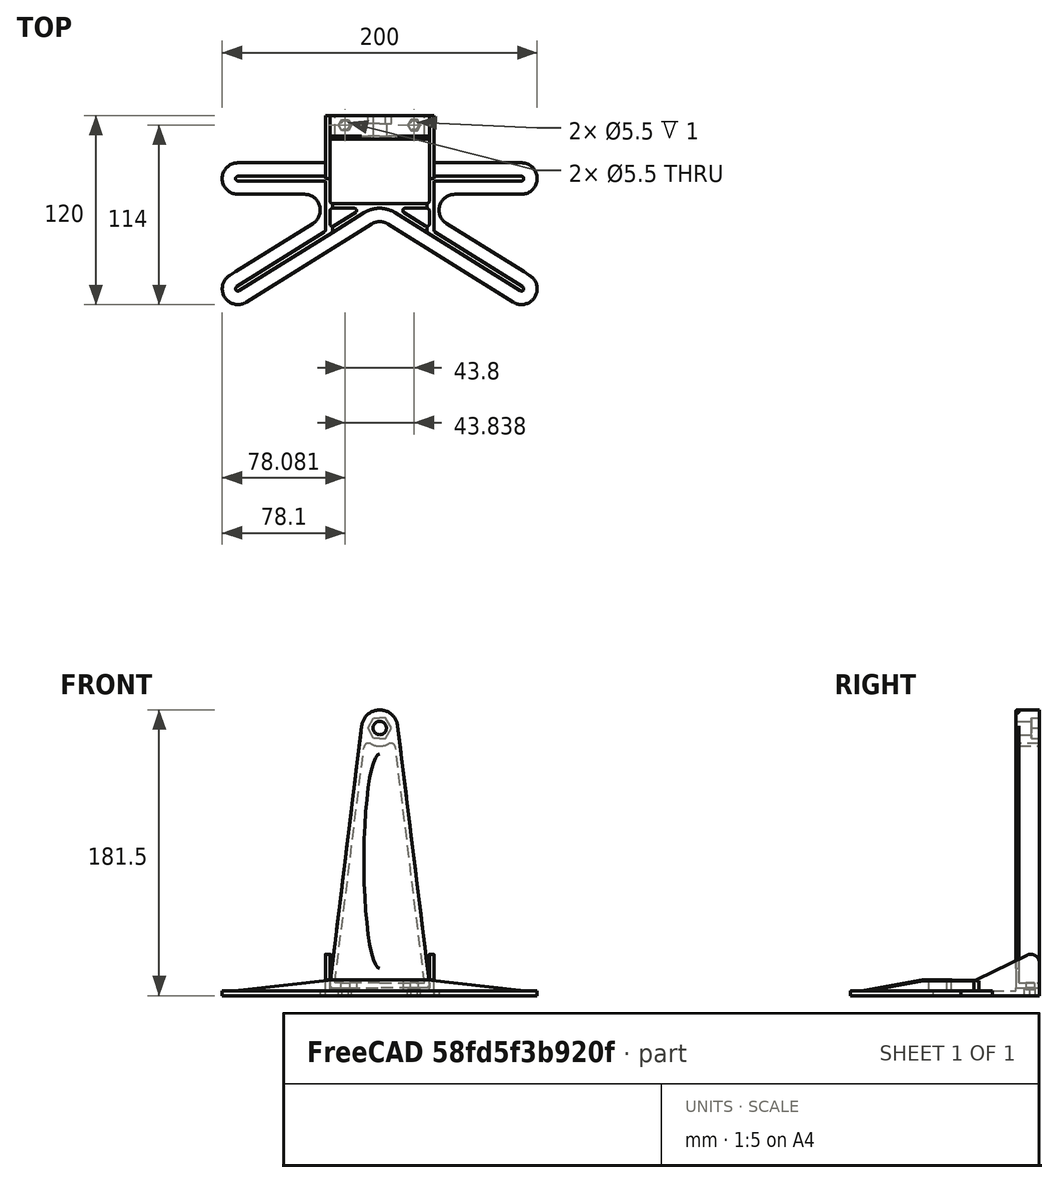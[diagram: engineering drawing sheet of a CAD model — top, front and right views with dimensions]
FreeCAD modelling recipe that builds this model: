
FCSTD DOCUMENT  (FreeCAD 0.19R24366 (Git))
Label: Ferris wheel foundation
License: All rights reserved
LicenseURL: http://en.wikipedia.org/wiki/All_rights_reserved
objects: Sketcher::SketchObject×14, PartDesign::Pad×6, PartDesign::Pocket×5, PartDesign::Mirrored×2, PartDesign::Body×2, PartDesign::SubtractivePipe×1, Mesh::Feature×1
note: 42 computed .brp shape members not serialized (recipe doc carries the construction recipe); baked Part::Feature solids carry a one-line shape summary decoded from their .brp

FEATURE [Sketcher::SketchObject] Sketch
  FullyConstrained = true
  MapMode = 5
  Support = -> [XY_Plane]
  sketch-geometry (16):
    g0: LineSegment StartX=0 StartY=0 StartZ=0 EndX=90 EndY=0 EndZ=0
    g1: LineSegment StartX=10 StartY=-20 StartZ=0 EndX=90 EndY=-70 EndZ=0
    g2: ArcOfCircle CenterX=90 CenterY=0 CenterZ=0 NormalX=0 NormalY=0 NormalZ=1 AngleXU=0 Radius=10 StartAngle=4.71239 EndAngle=7.85398
    g3: ArcOfCircle CenterX=90 CenterY=-70 CenterZ=0 NormalX=0 NormalY=0 NormalZ=1 AngleXU=0 Radius=10 StartAngle=4.15379 EndAngle=7.29539
    g4: ArcOfCircle CenterX=47.7359 CenterY=-20 CenterZ=0 NormalX=0 NormalY=0 NormalZ=1 AngleXU=0 Radius=10 StartAngle=1.5708 EndAngle=4.15379
    g5: ArcOfCircle CenterX=0 CenterY=-37.335 CenterZ=0 NormalX=0 NormalY=0 NormalZ=1 AngleXU=0 Radius=10 StartAngle=1.01219 EndAngle=1.5708
    g6: LineSegment StartX=47.7359 StartY=-10 StartZ=0 EndX=90 EndY=-10 EndZ=0
    g7: LineSegment StartX=42.436 StartY=-28.48 StartZ=0 EndX=95.3 EndY=-61.52 EndZ=0
    g8: LineSegment StartX=84.7 StartY=-78.48 StartZ=0 EndX=5.30001 EndY=-28.855 EndZ=0
    g9: LineSegment StartX=90 StartY=10 StartZ=0 EndX=31.5 EndY=10 EndZ=0
    g10: LineSegment StartX=0 StartY=10 StartZ=0 EndX=0 EndY=-27.335 EndZ=0
    g11: LineSegment StartX=10 StartY=-20 StartZ=0 EndX=0 EndY=-20 EndZ=0
    g12: LineSegment StartX=90 StartY=0 StartZ=0 EndX=100 EndY=0 EndZ=0
    g13: LineSegment StartX=31.5 StartY=10 StartZ=0 EndX=31.5 EndY=40 EndZ=0
    g14: LineSegment StartX=31.5 StartY=40 StartZ=0 EndX=0 EndY=40 EndZ=0
    g15: LineSegment StartX=0 StartY=40 StartZ=0 EndX=0 EndY=10 EndZ=0
  constraints (51):
    c: Coincident(g0,g-1)
    c: PointOnObject(g0,g-1)
    c: DistanceX(g0) = 90
    c: DistanceY(g1) = -70
    c: Vertical(g0,g1)
    c: Coincident(g2,g0)
    c: Coincident(g3,g1)
    c: PointOnObject(g5,g-2)
    c: PointOnObject(g5,g-2)
    c: Coincident(g6,g4)
    c: Coincident(g6,g2)
    c: Horizontal(g6)
    c: Coincident(g7,g4)
    c: Coincident(g7,g3)
    c: Coincident(g8,g3)
    c: Coincident(g8,g5)
    c: Coincident(g9,g2)
    c: PointOnObject(g10,g-2)
    c: Horizontal(g9)
    c: Coincident(g10,g5)
    c: Tangent(g2,g9)
    c: Tangent(g2,g6)
    c: Tangent(g4,g6)
    c: Tangent(g4,g7)
    c: Tangent(g7,g3)
    c: Tangent(g3,g8)
    c: Tangent(g8,g5)
    c: Parallel(g7,g1)
    c: Parallel(g1,g8)
    c: Equal(g5,g3)
    c: Equal(g3,g4)
    c: Equal(g4,g2)
    c: Horizontal(g4,g1)
    c: Diameter(g3) = 20
    c: Coincident(g11,g1)
    c: PointOnObject(g11,g10)
    c: Horizontal(g11)
    c: Coincident(g12,g2)
    c: PointOnObject(g12,g2)
    c: Horizontal(g12)
    c: Equal(g12,g11)
    c: Vertical(g13)
    c: Coincident(g14,g13)
    c: PointOnObject(g14,g-2)
    c: Horizontal(g14)
    c: Distance(g14) = 31.5
    c: Coincident(g15,g14)
    c: Coincident(g15,g10)
    c: Coincident(g9,g13)
    c: Distance(g15) = 30
    c: Horizontal(g10,g9)
FEATURE [Sketcher::SketchObject] Sketch001
  FullyConstrained = true
  MapMode = 5
  Support = -> [XY_Plane]
  expr: Constraints[34] = Sketch.Constraints[33]
  expr: Constraints[3] = Sketch.Constraints[3]
  expr: Constraints[2] = Sketch.Constraints[2]
  sketch-geometry (34):
    g0: LineSegment StartX=0 StartY=0 StartZ=0 EndX=90 EndY=0 EndZ=0
    g1: LineSegment StartX=10 StartY=-20 StartZ=0 EndX=90 EndY=-70 EndZ=0
    g2: ArcOfCircle CenterX=90 CenterY=0 CenterZ=0 NormalX=0 NormalY=0 NormalZ=1 AngleXU=0 Radius=10 StartAngle=4.71239 EndAngle=7.85398
    g3: ArcOfCircle CenterX=90 CenterY=-70 CenterZ=0 NormalX=0 NormalY=0 NormalZ=1 AngleXU=0 Radius=10 StartAngle=4.15379 EndAngle=7.29538
    g4: ArcOfCircle CenterX=47.7359 CenterY=-20 CenterZ=0 NormalX=0 NormalY=0 NormalZ=1 AngleXU=0 Radius=10 StartAngle=1.5708 EndAngle=4.15379
    g5: ArcOfCircle CenterX=0 CenterY=-37.335 CenterZ=0 NormalX=0 NormalY=0 NormalZ=1 AngleXU=0 Radius=10 StartAngle=1.0122 EndAngle=1.5708
    g6: LineSegment StartX=47.7359 StartY=-10 StartZ=0 EndX=90 EndY=-10 EndZ=0
    g7: LineSegment StartX=42.4359 StartY=-28.48 StartZ=0 EndX=95.3 EndY=-61.52 EndZ=0
    g8: LineSegment StartX=84.7 StartY=-78.48 StartZ=0 EndX=5.29999 EndY=-28.855 EndZ=0
    g9: LineSegment StartX=90 StartY=10 StartZ=0 EndX=0 EndY=10 EndZ=0
    g10: LineSegment StartX=0 StartY=10 StartZ=0 EndX=0 EndY=-27.335 EndZ=0
    g11: LineSegment StartX=10 StartY=-20 StartZ=0 EndX=0 EndY=-20 EndZ=0
    g12: LineSegment StartX=90 StartY=0 StartZ=0 EndX=100 EndY=0 EndZ=0
    g13: ArcOfCircle CenterX=90 CenterY=-70 CenterZ=0 NormalX=0 NormalY=0 NormalZ=1 AngleXU=0 Radius=1.5 StartAngle=4.15379 EndAngle=7.29538
    g14: ArcOfCircle CenterX=90 CenterY=0 CenterZ=0 NormalX=0 NormalY=0 NormalZ=1 AngleXU=0 Radius=1.5 StartAngle=4.71239 EndAngle=7.85398
    g15: ArcOfCircle CenterX=0 CenterY=-37.335 CenterZ=0 NormalX=0 NormalY=0 NormalZ=1 AngleXU=0 Radius=18.5 StartAngle=1.0122 EndAngle=1.5708
    g16: LineSegment StartX=34.5 StartY=-1.5 StartZ=0 EndX=90 EndY=-1.5 EndZ=0
    g17: LineSegment StartX=90.795 StartY=-68.728 StartZ=0 EndX=35.205 EndY=-33.9843 EndZ=0
    g18: LineSegment StartX=89.205 StartY=-71.272 StartZ=0 EndX=9.80498 EndY=-21.647 EndZ=0
    g19: LineSegment StartX=90 StartY=1.5 StartZ=0 EndX=34.5 EndY=1.5 EndZ=0
    g20: LineSegment StartX=0 StartY=-15.835 StartZ=0 EndX=30 EndY=-15.835 EndZ=0
    g21: ArcOfCircle CenterX=30 CenterY=-14.335 CenterZ=0 NormalX=0 NormalY=0 NormalZ=1 AngleXU=0 Radius=1.5 StartAngle=4.71239 EndAngle=6.28319
    g22: LineSegment StartX=1.1e-15 StartY=-18.835 StartZ=0 EndX=0 EndY=-15.835 EndZ=0
    g23: LineSegment StartX=15.4013 StartY=-21.607 StartZ=0 EndX=29.205 EndY=-30.2343 EndZ=0
    g24: LineSegment StartX=16.1963 StartY=-18.835 StartZ=0 EndX=30 EndY=-18.835 EndZ=0
    g25: ArcOfCircle CenterX=16.1963 CenterY=-20.335 CenterZ=0 NormalX=0 NormalY=0 NormalZ=1 AngleXU=0 Radius=1.5 StartAngle=1.5708 EndAngle=4.15379
    g26: ArcOfCircle CenterX=30 CenterY=-20.335 CenterZ=0 NormalX=0 NormalY=0 NormalZ=1 AngleXU=0 Radius=1.5 StartAngle=3.41034e-06 EndAngle=1.5708
    g27: ArcOfCircle CenterX=30 CenterY=-28.9623 CenterZ=0 NormalX=0 NormalY=0 NormalZ=1 AngleXU=0 Radius=1.5 StartAngle=4.15379 EndAngle=6.28319
    g28: LineSegment StartX=34.5 StartY=40 StartZ=0 EndX=31.5 EndY=40 EndZ=0
    g29: LineSegment StartX=31.5 StartY=40 StartZ=0 EndX=31.5 EndY=-14.335 EndZ=0
    g30: LineSegment StartX=34.5 StartY=1.5 StartZ=0 EndX=34.5 EndY=40 EndZ=0
    g31: LineSegment StartX=34.5 StartY=-32.7123 StartZ=0 EndX=34.5 EndY=-1.5 EndZ=0
    g32: ArcOfCircle CenterX=36 CenterY=-32.7123 CenterZ=0 NormalX=0 NormalY=0 NormalZ=1 AngleXU=0 Radius=1.5 StartAngle=3.14159 EndAngle=4.15379
    g33: LineSegment StartX=31.5 StartY=-20.3349 StartZ=0 EndX=31.5 EndY=-28.9623 EndZ=0
  constraints (109):
    c: Coincident(g0,g-1)
    c: PointOnObject(g0,g-1)
    c: DistanceX(g0) = 90
    c: DistanceY(g1) = -70
    c: Vertical(g0,g1)
    c: Coincident(g2,g0)
    c: Coincident(g3,g1)
    c: PointOnObject(g5,g-2)
    c: PointOnObject(g5,g-2)
    c: Coincident(g6,g4)
    c: Coincident(g6,g2)
    c: Horizontal(g6)
    c: Coincident(g7,g4)
    c: Coincident(g7,g3)
    c: Coincident(g8,g3)
    c: Coincident(g8,g5)
    c: Coincident(g9,g2)
    c: PointOnObject(g9,g-2)
    c: Horizontal(g9)
    c: Coincident(g10,g9)
    c: Coincident(g10,g5)
    c: Tangent(g2,g9)
    c: Tangent(g2,g6)
    c: Tangent(g4,g6)
    c: Tangent(g4,g7)
    c: Tangent(g7,g3)
    c: Tangent(g3,g8)
    c: Tangent(g8,g5)
    c: Parallel(g7,g1)
    c: Parallel(g1,g8)
    c: Equal(g5,g3)
    c: Equal(g3,g4)
    c: Equal(g4,g2)
    c: Horizontal(g4,g1)
    c: Diameter(g3) = 20
    c: Coincident(g11,g1)
    c: PointOnObject(g11,g10)
    c: Horizontal(g11)
    c: Coincident(g12,g2)
    c: PointOnObject(g12,g2)
    c: Horizontal(g12)
    c: Equal(g12,g11)
    c: Coincident(g13,g1)
    c: Coincident(g14,g0)
    c: Coincident(g15,g5)
    c: PointOnObject(g15,g10)
    c: Coincident(g16,g14)
    c: Horizontal(g16)
    c: Coincident(g17,g13)
    c: Coincident(g18,g13)
    c: Coincident(g18,g15)
    c: Parallel(g17,g1)
    c: Parallel(g18,g1)
    c: Tangent(g13,g17)
    c: Tangent(g13,g18)
    c: Diameter(g13) = 3
    c: Equal(g13,g14)
    c: Tangent(g14,g16)
    c: Coincident(g19,g14)
    c: Horizontal(g19)
    c: PointOnObject(g20,g10)
    c: Horizontal(g20)
    c: Coincident(g21,g20)
    c: Tangent(g18,g15)
    c: Tangent(g20,g21)
    c: Coincident(g22,g15)
    c: Coincident(g22,g20)
    c: Distance(g22) = 3
    c: Coincident(g25,g24)
    c: Coincident(g25,g23)
    c: Coincident(g26,g24)
    c: Coincident(g27,g23)
    c: Tangent(g24,g25)
    c: Tangent(g25,g23)
    c: Tangent(g24,g26)
    c: Tangent(g27,g23)
    c: Horizontal(g24)
    c: Equal(g26,g25)
    c: Equal(g25,g27)
    c: Tangent(g17,g23)
    c: Equal(g27,g13)
    c: PointOnObject(g15,g24)
    c: Tangent(g14,g19)
    c: Equal(g26,g21)
    c: Coincident(g28,g29)
    c: Coincident(g30,g28)
    c: Horizontal(g28)
    c: Vertical(g29)
    c: Vertical(g30)
    c: DistanceY(g28) = 40
    c: Distance(g28) = 3
    c: DistanceX(g28) = 31.5
    c: Coincident(g21,g29)
    c: Coincident(g19,g30)
    c: Vertical(g31)
    c: Coincident(g31,g16)
    c: Vertical(g16,g19)
    c: Tangent(g21,g29)
    c: Coincident(g32,g17)
    c: Coincident(g32,g31)
    c: Tangent(g17,g32)
    c: Tangent(g32,g31)
    c: Coincident(g33,g26)
    c: Vertical(g33)
    c: Vertical(g21,g26)
    c: Coincident(g27,g33)
    c: Tangent(g33,g27)
    c: Equal(g32,g27)
    c: Tangent(g33,g26)
FEATURE [PartDesign::Pad] Pad
  Direction = (1,1,1)
  Length = 3
  Length2 = 100
  Profile = -> Sketch
  Type = 0
FEATURE [PartDesign::Pad] Pad001
  BaseFeature = -> Pad
  Direction = (1,1,1)
  Length = 10
  Length2 = 100
  Profile = -> Sketch001
  Type = 0
FEATURE [Sketcher::SketchObject] Sketch002
  FullyConstrained = true
  MapMode = 5
  Placement = pos=(0,0,0) rot=(1,0,0;1.5708rad)
  Support = -> [XZ_Plane001]
  sketch-geometry (21):
    g0: LineSegment StartX=7.50555 StartY=165 StartZ=0 EndX=3.75278 EndY=171.5 EndZ=0
    g1: LineSegment StartX=3.75278 StartY=171.5 StartZ=0 EndX=-3.75278 EndY=171.5 EndZ=0
    g2: LineSegment StartX=-3.75278 StartY=171.5 StartZ=0 EndX=-7.50555 EndY=165 EndZ=0
    g3: LineSegment StartX=-7.50555 StartY=165 StartZ=0 EndX=-3.75278 EndY=158.5 EndZ=0
    g4: LineSegment StartX=-3.75278 StartY=158.5 StartZ=0 EndX=3.75278 EndY=158.5 EndZ=0
    g5: LineSegment StartX=3.75278 StartY=158.5 StartZ=0 EndX=7.50555 EndY=165 EndZ=0
    g6: Circle CenterX=0 CenterY=165 CenterZ=0 NormalX=0 NormalY=0 NormalZ=1 AngleXU=0 Radius=7.50555
    g7: ArcOfCircle CenterX=0 CenterY=165 CenterZ=0 NormalX=0 NormalY=0 NormalZ=1 AngleXU=0 Radius=11.5 StartAngle=0.122446 EndAngle=1.5708
    g8: LineSegment StartX=11.4139 StartY=166.405 StartZ=0 EndX=31.4775 EndY=3.36703 EndZ=0
    g9: LineSegment StartX=31.5 StartY=3 StartZ=0 EndX=31.5 EndY=0 EndZ=0
    g10: ArcOfCircle CenterX=28.495 CenterY=3 CenterZ=0 NormalX=0 NormalY=0 NormalZ=1 AngleXU=0 Radius=3.005 StartAngle=6.28319 EndAngle=6.40563
    g11: ArcOfEllipse CenterX=0 CenterY=80.375 CenterZ=0 NormalX=0 NormalY=0 NormalZ=1 MajorRadius=68.125 MinorRadius=10 AngleXU=-1.5708 StartAngle=0 EndAngle=3.14159
    g12: LineSegment StartX=0 StartY=12.25 StartZ=0 EndX=0 EndY=148.5 EndZ=0
    g13: LineSegment StartX=10 StartY=80.375 StartZ=0 EndX=-10 EndY=80.375 EndZ=0
    g14: GeomPoint X=0 Y=12.9879 Z=0
    g15: GeomPoint X=0 Y=147.762 Z=0
    g16: LineSegment StartX=31.5 StartY=0 StartZ=0 EndX=0 EndY=0 EndZ=0
    g17: LineSegment StartX=0 StartY=12.25 StartZ=0 EndX=0 EndY=0 EndZ=0
    g18: LineSegment StartX=1.2e-15 StartY=148.5 StartZ=0 EndX=-8e-16 EndY=160.75 EndZ=0
    g19: LineSegment StartX=0 StartY=176.5 StartZ=0 EndX=0 EndY=169.25 EndZ=0
    g20: ArcOfCircle CenterX=0 CenterY=165 CenterZ=0 NormalX=0 NormalY=0 NormalZ=1 AngleXU=0 Radius=4.25 StartAngle=4.71239 EndAngle=7.85398
  constraints (52):
    c: Coincident(g0,g1)
    c: Coincident(g1,g2)
    c: Coincident(g2,g3)
    c: Coincident(g3,g4)
    c: Coincident(g4,g5)
    c: Coincident(g5,g0)
    c: Equal(g0, g1-g5) x5
    c: PointOnObject(g0,g6)
    c: PointOnObject(g1,g6)
    c: PointOnObject(g2,g6)
    c: PointOnObject(g3,g6)
    c: PointOnObject(g4,g6)
    c: PointOnObject(g5,g6)
    c: PointOnObject(g6,g-2)
    c: Horizontal(g1)
    c: DistanceY(g4,g0) = 13
    c: Coincident(g7,g6)
    c: PointOnObject(g7,g-2)
    c: Coincident(g8,g7)
    c: PointOnObject(g9,g-1)
    c: Vertical(g9)
    c: Coincident(g10,g9)
    c: Coincident(g10,g8)
    c: InternalAlignment(g12-g15 -> g11) x4
    c: PointOnObject(g11,g-2)
    c: PointOnObject(g11,g-2)
    c: Vertical(g12)
    c: Distance(g13) = 20
    c: DistanceY(g7) = 165
    c: Diameter(g6) = 15.0111
    c: Diameter(g7) = 23
    c: Tangent(g8,g7)
    c: Coincident(g16,g9)
    c: Coincident(g16,g-1)
    c: PointOnObject(g11,g-2)
    c: Coincident(g17,g11)
    c: Coincident(g17,g16)
    c: Coincident(g18,g11)
    c: PointOnObject(g18,g-2)
    c: Coincident(g19,g7)
    c: PointOnObject(g19,g-2)
    c: Coincident(g20,g7)
    c: Coincident(g20,g18)
    c: Coincident(g20,g19)
    c: Diameter(g20) = 8.5
    c: Distance(g16) = 31.5
    c: Distance(g11,g4) = 10
    c: Equal(g17,g18)
    c: Tangent(g10,g8)
    c: Tangent(g10,g9)
    c: Distance(g9) = 3
    c: Diameter(g10) = 6.01
FEATURE [Sketcher::SketchObject] Sketch003
  AttachmentOffset = pos=(0,0,2) rot=(0,0,1;0rad)
  FullyConstrained = true
  MapMode = 5
  Placement = pos=(0,-2,4e-16) rot=(1,0,0;1.5708rad)
  Support = -> [XZ_Plane001]
  expr: .AttachmentOffset.Base.z = Pad002.Length
  expr: Constraints[52] = Sketch002.Constraints[57]
  expr: Constraints[48] = Sketch002.Constraints[53]
  expr: Constraints[15] = Sketch002.Constraints[19]
  expr: Constraints[33] = Sketch002.Constraints[37]
  expr: Constraints[46] = Sketch002.Constraints[51]
  expr: Constraints[47] = Sketch002.Constraints[52]
  expr: Constraints[31] = Sketch002.Constraints[35]
  expr: Constraints[30] = Sketch002.Constraints[34]
  sketch-geometry (31):
    g0: LineSegment StartX=7.50555 StartY=165 StartZ=0 EndX=3.75278 EndY=171.5 EndZ=0
    g1: LineSegment StartX=3.75278 StartY=171.5 StartZ=0 EndX=0 EndY=171.5 EndZ=0
    g2: LineSegment StartX=-3.75278 StartY=171.5 StartZ=0 EndX=-7.50555 EndY=165 EndZ=0
    g3: LineSegment StartX=-7.50555 StartY=165 StartZ=0 EndX=-3.75278 EndY=158.5 EndZ=0
    g4: LineSegment StartX=0 StartY=158.5 StartZ=0 EndX=3.75278 EndY=158.5 EndZ=0
    g5: LineSegment StartX=3.75278 StartY=158.5 StartZ=0 EndX=7.50555 EndY=165 EndZ=0
    g6: Circle CenterX=0 CenterY=165 CenterZ=0 NormalX=0 NormalY=0 NormalZ=1 AngleXU=0 Radius=7.50555
    g7: ArcOfCircle CenterX=0 CenterY=165 CenterZ=0 NormalX=0 NormalY=0 NormalZ=1 AngleXU=0 Radius=11.5 StartAngle=0.122445 EndAngle=1.5708
    g8: LineSegment StartX=11.4139 StartY=166.405 StartZ=0 EndX=31.4775 EndY=3.36642 EndZ=0
    g9: LineSegment StartX=31.5 StartY=3 StartZ=0 EndX=31.5 EndY=0 EndZ=0
    g10: ArcOfCircle CenterX=28.5 CenterY=3 CenterZ=0 NormalX=0 NormalY=0 NormalZ=1 AngleXU=0 Radius=3 StartAngle=6.28319 EndAngle=6.40563
    g11: ArcOfEllipse CenterX=0 CenterY=80.375 CenterZ=0 NormalX=0 NormalY=0 NormalZ=1 MajorRadius=68.125 MinorRadius=10 AngleXU=-1.5708 StartAngle=0 EndAngle=3.14159
    g12: LineSegment StartX=0 StartY=12.25 StartZ=0 EndX=0 EndY=148.5 EndZ=0
    g13: LineSegment StartX=10 StartY=80.375 StartZ=0 EndX=-10 EndY=80.375 EndZ=0
    g14: GeomPoint X=0 Y=12.9879 Z=0
    g15: GeomPoint X=0 Y=147.762 Z=0
    g16: LineSegment StartX=31.5 StartY=0 StartZ=0 EndX=0 EndY=0 EndZ=0
    g17: LineSegment StartX=0 StartY=12.25 StartZ=0 EndX=0 EndY=0 EndZ=0
    g18: LineSegment StartX=0 StartY=148.5 StartZ=0 EndX=0 EndY=160.75 EndZ=0
    g19: LineSegment StartX=0 StartY=176.5 StartZ=0 EndX=0 EndY=171.5 EndZ=0
    g20: ArcOfCircle CenterX=0 CenterY=165 CenterZ=0 NormalX=0 NormalY=0 NormalZ=1 AngleXU=0 Radius=4.25 StartAngle=4.71239 EndAngle=7.85398
    g21: LineSegment StartX=-3.75278 StartY=171.5 StartZ=0 EndX=-3.75278 EndY=158.5 EndZ=0
    g22: LineSegment StartX=3.75278 StartY=158.5 StartZ=0 EndX=-7.50555 EndY=165 EndZ=0
    g23: LineSegment StartX=0 StartY=0 StartZ=0 EndX=0 EndY=3 EndZ=0
    g24: LineSegment StartX=0 StartY=3 StartZ=0 EndX=28.5 EndY=3 EndZ=0
    g25: LineSegment StartX=28.5 StartY=3 StartZ=0 EndX=10.075 EndY=152.722 EndZ=0
    g26: ArcOfCircle CenterX=0 CenterY=165 CenterZ=0 NormalX=0 NormalY=0 NormalZ=1 AngleXU=0 Radius=11.5 StartAngle=4.71239 EndAngle=5.22389
    g27: ArcOfCircle CenterX=7.0975 CenterY=152.356 CenterZ=0 NormalX=0 NormalY=0 NormalZ=1 AngleXU=0 Radius=3 StartAngle=0.122445 EndAngle=2.08229
    g28: LineSegment StartX=0 StartY=153.5 StartZ=0 EndX=0 EndY=158.5 EndZ=0
    g29: LineSegment StartX=0 StartY=171.5 StartZ=0 EndX=0 EndY=169.25 EndZ=0
    g30: LineSegment StartX=0 StartY=160.75 StartZ=0 EndX=0 EndY=158.5 EndZ=0
  constraints (83):
    c: Coincident(g0,g1)
    c: Coincident(g2,g3)
    c: Coincident(g4,g5)
    c: Coincident(g5,g0)
    c: Equal(g0,g2)
    c: Equal(g0,g3)
    c: Equal(g0,g5)
    c: PointOnObject(g0,g6)
    c: PointOnObject(g2,g6)
    c: PointOnObject(g2,g6)
    c: PointOnObject(g3,g6)
    c: PointOnObject(g4,g6)
    c: PointOnObject(g5,g6)
    c: PointOnObject(g6,g-2)
    c: Horizontal(g1)
    c: DistanceY(g4,g0) = 13
    c: Coincident(g7,g6)
    c: PointOnObject(g7,g-2)
    c: Coincident(g8,g7)
    c: PointOnObject(g9,g-1)
    c: Vertical(g9)
    c: Coincident(g10,g9)
    c: Coincident(g10,g8)
    c: InternalAlignment(g12-g15 -> g11) x4
    c: PointOnObject(g11,g-2)
    c: PointOnObject(g11,g-2)
    c: Vertical(g12)
    c: Distance(g13) = 20
    c: DistanceY(g7) = 165
    c: Diameter(g6) = 15.0111
    c: Diameter(g7) = 23
    c: Tangent(g8,g7)
    c: Coincident(g16,g9)
    c: Coincident(g16,g-1)
    c: PointOnObject(g11,g-2)
    c: Coincident(g17,g11)
    c: Coincident(g17,g16)
    c: Coincident(g18,g11)
    c: PointOnObject(g18,g-2)
    c: Coincident(g19,g7)
    c: PointOnObject(g20,g-2)
    c: Coincident(g20,g7)
    c: Coincident(g20,g18)
    c: Diameter(g20) = 8.5
    c: Distance(g16) = 31.5
    c: Distance(g11,g4) = 10
    c: Equal(g17,g18)
    c: Tangent(g10,g8)
    c: Tangent(g10,g9)
    c: Distance(g9) = 3
    c: PointOnObject(g4,g18)
    c: Horizontal(g1,g2)
    c: Horizontal(g4,g3)
    c: Equal(g4,g1)
    c: Coincident(g19,g1)
    c: Vertical(g19)
    c: Coincident(g21,g2)
    c: Coincident(g21,g3)
    c: Coincident(g22,g4)
    c: Coincident(g22,g2)
    c: Equal(g21,g22)
    c: Coincident(g23,g16)
    c: PointOnObject(g23,g17)
    c: Coincident(g24,g23)
    c: Coincident(g24,g10)
    c: Horizontal(g24)
    c: Coincident(g25,g10)
    c: Coincident(g26,g7)
    c: PointOnObject(g26,g18)
    c: Coincident(g27,g25)
    c: Coincident(g27,g26)
    c: Equal(g26,g7)
    c: Tangent(g26,g27)
    c: Tangent(g27,g25)
    c: Parallel(g25,g8)
    c: Diameter(g10) = 6
    c: Equal(g27,g10)
    c: Coincident(g28,g26)
    c: Coincident(g28,g4)
    c: Coincident(g29,g19)
    c: Coincident(g29,g20)
    c: Coincident(g30,g18)
    c: Coincident(g30,g28)
FEATURE [PartDesign::Pad] Pad002
  Direction = (1,1,1)
  Length = 2
  Length2 = 100
  Placement = pos=(0,0,0) rot=(1,0,0;1.5708rad)
  Profile = -> Sketch002
  Type = 0
FEATURE [PartDesign::Pad] Pad003
  BaseFeature = -> Pad002
  Direction = (1,1,1)
  Length = 13
  Length2 = 100
  Placement = pos=(0,0,0) rot=(1,0,0;1.5708rad)
  Profile = -> Sketch003
  Type = 0
  expr: Length = 15mm - Pad002.Length
FEATURE [Sketcher::SketchObject] Sketch004
  FullyConstrained = false
  MapMode = 5
  Support = -> [XY_Plane001]
  sketch-geometry (1):
    g0: Circle CenterX=21.9188 CenterY=-9 CenterZ=0 NormalX=0 NormalY=0 NormalZ=1 AngleXU=0 Radius=2.75
  constraints (2):
    c: Diameter(g0) = 5.5
    c: DistanceY(g0) = -9
FEATURE [PartDesign::Pocket] Pocket
  BaseFeature = -> Pad003
  Length = 5
  Length2 = 100
  Placement = pos=(0,0,0) rot=(1,0,0;1.5708rad)
  Profile = -> Sketch004
  Reversed = true
  Type = 2
FEATURE [Sketcher::SketchObject] Sketch005
  AttachmentOffset = pos=(0,0,10) rot=(0,0,1;0rad)
  FullyConstrained = true
  MapMode = 5
  Placement = pos=(0,-10,2.2e-15) rot=(1,0,0;1.5708rad)
  Support = -> [XZ_Plane001]
  expr: Constraints[58] = Sketch002.Constraints[58]
  expr: Constraints[57] = Sketch002.Constraints[57]
  expr: Constraints[53] = Sketch002.Constraints[53]
  expr: Constraints[52] = Sketch002.Constraints[52]
  expr: Constraints[51] = Sketch002.Constraints[51]
  expr: Constraints[37] = Sketch002.Constraints[37]
  expr: Constraints[35] = Sketch002.Constraints[35]
  expr: Constraints[34] = Sketch002.Constraints[34]
  expr: Constraints[19] = Sketch002.Constraints[19]
  sketch-geometry (21):
    g0: LineSegment StartX=7.50555 StartY=165 StartZ=0 EndX=3.75278 EndY=171.5 EndZ=0
    g1: LineSegment StartX=3.75278 StartY=171.5 StartZ=0 EndX=-3.75278 EndY=171.5 EndZ=0
    g2: LineSegment StartX=-3.75278 StartY=171.5 StartZ=0 EndX=-7.50555 EndY=165 EndZ=0
    g3: LineSegment StartX=-7.50555 StartY=165 StartZ=0 EndX=-3.75278 EndY=158.5 EndZ=0
    g4: LineSegment StartX=-3.75278 StartY=158.5 StartZ=0 EndX=3.75278 EndY=158.5 EndZ=0
    g5: LineSegment StartX=3.75278 StartY=158.5 StartZ=0 EndX=7.50555 EndY=165 EndZ=0
    g6: Circle CenterX=0 CenterY=165 CenterZ=0 NormalX=0 NormalY=0 NormalZ=1 AngleXU=0 Radius=7.50555
    g7: ArcOfCircle CenterX=0 CenterY=165 CenterZ=0 NormalX=0 NormalY=0 NormalZ=1 AngleXU=0 Radius=11.5 StartAngle=0.122446 EndAngle=1.5708
    g8: LineSegment StartX=11.4139 StartY=166.405 StartZ=0 EndX=31.4775 EndY=3.36703 EndZ=0
    g9: LineSegment StartX=31.5 StartY=3 StartZ=0 EndX=31.5 EndY=0 EndZ=0
    g10: ArcOfCircle CenterX=28.495 CenterY=3 CenterZ=0 NormalX=0 NormalY=0 NormalZ=1 AngleXU=0 Radius=3.005 StartAngle=6.28319 EndAngle=6.40563
    g11: ArcOfEllipse CenterX=0 CenterY=80.375 CenterZ=0 NormalX=0 NormalY=0 NormalZ=1 MajorRadius=68.125 MinorRadius=10 AngleXU=-1.5708 StartAngle=0 EndAngle=3.14159
    g12: LineSegment StartX=0 StartY=12.25 StartZ=0 EndX=0 EndY=148.5 EndZ=0
    g13: LineSegment StartX=10 StartY=80.375 StartZ=0 EndX=-10 EndY=80.375 EndZ=0
    g14: GeomPoint X=0 Y=12.9879 Z=0
    g15: GeomPoint X=0 Y=147.762 Z=0
    g16: LineSegment StartX=31.5 StartY=0 StartZ=0 EndX=0 EndY=0 EndZ=0
    g17: LineSegment StartX=0 StartY=12.25 StartZ=0 EndX=0 EndY=0 EndZ=0
    g18: LineSegment StartX=0 StartY=148.5 StartZ=0 EndX=0 EndY=160.75 EndZ=0
    g19: LineSegment StartX=0 StartY=176.5 StartZ=0 EndX=0 EndY=169.25 EndZ=0
    g20: ArcOfCircle CenterX=0 CenterY=165 CenterZ=0 NormalX=0 NormalY=0 NormalZ=1 AngleXU=0 Radius=4.25 StartAngle=4.71239 EndAngle=7.85398
  constraints (52):
    c: Coincident(g0,g1)
    c: Coincident(g1,g2)
    c: Coincident(g2,g3)
    c: Coincident(g3,g4)
    c: Coincident(g4,g5)
    c: Coincident(g5,g0)
    c: Equal(g0, g1-g5) x5
    c: PointOnObject(g0,g6)
    c: PointOnObject(g1,g6)
    c: PointOnObject(g2,g6)
    c: PointOnObject(g3,g6)
    c: PointOnObject(g4,g6)
    c: PointOnObject(g5,g6)
    c: PointOnObject(g6,g-2)
    c: Horizontal(g1)
    c: DistanceY(g4,g0) = 13
    c: Coincident(g7,g6)
    c: PointOnObject(g7,g-2)
    c: Coincident(g8,g7)
    c: PointOnObject(g9,g-1)
    c: Vertical(g9)
    c: Coincident(g10,g9)
    c: Coincident(g10,g8)
    c: InternalAlignment(g12-g15 -> g11) x4
    c: PointOnObject(g11,g-2)
    c: PointOnObject(g11,g-2)
    c: Vertical(g12)
    c: Distance(g13) = 20
    c: DistanceY(g7) = 165
    c: Diameter(g6) = 15.0111
    c: Diameter(g7) = 23
    c: Tangent(g8,g7)
    c: Coincident(g16,g9)
    c: Coincident(g16,g-1)
    c: PointOnObject(g11,g-2)
    c: Coincident(g17,g11)
    c: Coincident(g17,g16)
    c: Coincident(g18,g11)
    c: PointOnObject(g18,g-2)
    c: Coincident(g19,g7)
    c: PointOnObject(g19,g-2)
    c: Coincident(g20,g7)
    c: Coincident(g20,g18)
    c: Coincident(g20,g19)
    c: Diameter(g20) = 8.5
    c: Distance(g16) = 31.5
    c: Distance(g11,g4) = 10
    c: Equal(g17,g18)
    c: Tangent(g10,g8)
    c: Tangent(g10,g9)
    c: Distance(g9) = 3
    c: Diameter(g10) = 6.01
FEATURE [Sketcher::SketchObject] Sketch006
  FullyConstrained = false
  MapMode = 5
  Placement = pos=(0,0,0) rot=(0.57735,0.57735,0.57735;2.0944rad)
  Support = -> [YZ_Plane001]
  sketch-geometry (5):
    g0: LineSegment StartX=0 StartY=0 StartZ=0 EndX=-1.00001 EndY=3.09469e-11 EndZ=0
    g1: ArcOfCircle CenterX=-1 CenterY=1 CenterZ=0 NormalX=0 NormalY=0 NormalZ=1 AngleXU=0 Radius=1 StartAngle=4.71238 EndAngle=6.28319
    g2: LineSegment StartX=-3.09138e-11 StartY=1.00001 StartZ=0 EndX=0.593354 EndY=1.00001 EndZ=0
    g3: LineSegment StartX=0.593354 StartY=1.00001 StartZ=0 EndX=0.593354 EndY=0 EndZ=0
    g4: LineSegment StartX=0.593354 StartY=0 StartZ=0 EndX=0 EndY=0 EndZ=0
  constraints (14):
    c: Coincident(g0,g-1)
    c: PointOnObject(g0,g-1)
    c: PointOnObject(g1,g-2)
    c: Coincident(g1,g0)
    c: Tangent(g1,g0)
    c: Diameter(g1) = 2
    c: Coincident(g2,g1)
    c: Horizontal(g2)
    c: Coincident(g3,g2)
    c: PointOnObject(g3,g-1)
    c: Vertical(g3)
    c: Coincident(g4,g3)
    c: Coincident(g4,g0)
    c: Tangent(g-2,g1)
FEATURE [PartDesign::Pocket] Pocket001
  BaseFeature = -> Pocket
  Length = 5
  Length2 = 100
  Placement = pos=(0,0,0) rot=(1,0,0;1.5708rad)
  Profile = -> Sketch005
  Reversed = true
  Type = 0
FEATURE [PartDesign::SubtractivePipe] SubtractivePipe
  AuxilleryCurvelinear = true
  AuxillerySpineTangent = false
  BaseFeature = -> Pocket001
  Binormal = (0,0,0)
  Mode = 0
  Placement = pos=(0,0,0) rot=(1,0,0;1.5708rad)
  Profile = -> Sketch006
  Spine = -> Pocket001 [Edge18,Edge6,Edge3,Edge9,Edge12]
  SpineTangent = false
  Transformation = 0
  Transition = 1
FEATURE [PartDesign::Mirrored] Mirrored001
  BaseFeature = -> SubtractivePipe
  MirrorPlane = -> Sketch002 [V_Axis]
  Originals = -> [Pad002,Pad003,Pocket,Pocket001,SubtractivePipe]
  Placement = pos=(0,0,0) rot=(1,0,0;1.5708rad)
FEATURE [Sketcher::SketchObject] Sketch007
  FullyConstrained = true
  MapMode = 5
  Support = -> [XY_Plane001]
  sketch-geometry (4):
    g0: LineSegment StartX=0 StartY=0 StartZ=0 EndX=31.5 EndY=0 EndZ=0
    g1: LineSegment StartX=31.5 StartY=0 StartZ=0 EndX=31.5 EndY=-15 EndZ=0
    g2: LineSegment StartX=31.5 StartY=-15 StartZ=0 EndX=0 EndY=-15 EndZ=0
    g3: LineSegment StartX=0 StartY=-15 StartZ=0 EndX=0 EndY=0 EndZ=0
  constraints (11):
    c: Coincident(g0,g1)
    c: Coincident(g1,g2)
    c: Coincident(g2,g3)
    c: Coincident(g3,g0)
    c: Horizontal(g0)
    c: Horizontal(g2)
    c: Vertical(g1)
    c: Vertical(g3)
    c: Coincident(g0,g-1)
    c: Distance(g3) = 15
    c: Distance(g0) = 31.5
FEATURE [PartDesign::Body] Body001
  Group = -> [Sketch002,Sketch003,Pad002,Pad003,Sketch004,Pocket,Sketch005,Sketch006,Pocket001,SubtractivePipe,Mirrored001,Sketch007]
  Origin = -> Origin001
  Placement = pos=(0,25,5) rot=(0,0,1;3.14159rad)
  Tip = -> Mirrored001
FEATURE [Sketcher::SketchObject] Sketch008
  AttachmentOffset = pos=(0,30,0) rot=(0,0,1;0rad)
  FullyConstrained = true
  MapMode = 5
  Placement = pos=(0,30,0) rot=(0,0,1;0rad)
  Support = -> [XY_Plane]
  sketch-geometry (4):
    g0: LineSegment StartX=0 StartY=-5 StartZ=0 EndX=31.5 EndY=-5 EndZ=0
    g1: LineSegment StartX=31.5 StartY=-5 StartZ=0 EndX=31.5 EndY=10 EndZ=0
    g2: LineSegment StartX=31.5 StartY=10 StartZ=0 EndX=0 EndY=10 EndZ=0
    g3: LineSegment StartX=0 StartY=10 StartZ=0 EndX=0 EndY=-5 EndZ=0
  constraints (12):
    c: Coincident(g0,g1)
    c: Coincident(g1,g2)
    c: Coincident(g2,g3)
    c: Coincident(g3,g0)
    c: Horizontal(g0)
    c: Horizontal(g2)
    c: Vertical(g1)
    c: Vertical(g3)
    c: PointOnObject(g0,g-2)
    c: Distance(g3) = 15
    c: Distance(g2) = 31.5
    c: DistanceY(g2) = 10
FEATURE [Sketcher::SketchObject] Sketch009
  AttachmentOffset = pos=(0,30,0) rot=(0,0,1;0rad)
  FullyConstrained = true
  MapMode = 5
  Placement = pos=(0,30,0) rot=(0,0,1;0rad)
  Support = -> [XY_Plane]
  sketch-geometry (1):
    g0: Circle CenterX=21.9 CenterY=4 CenterZ=0 NormalX=0 NormalY=0 NormalZ=1 AngleXU=0 Radius=2.75
  constraints (3):
    c: DistanceX(g0) = 21.9
    c: Diameter(g0) = 5.5
    c: DistanceY(g0) = 4
FEATURE [PartDesign::Pad] Pad004
  BaseFeature = -> Pad001
  Direction = (1,1,1)
  Length = 5
  Length2 = 100
  Profile = -> Sketch008
  Type = 0
FEATURE [PartDesign::Pocket] Pocket002
  BaseFeature = -> Pad004
  Length = 5
  Length2 = 100
  Midplane = true
  Profile = -> Sketch009
  Type = 1
FEATURE [Sketcher::SketchObject] Sketch010
  FullyConstrained = true
  MapMode = 5
  Placement = pos=(0,0,0) rot=(1,0,0;1.5708rad)
  Support = -> [XZ_Plane]
  sketch-geometry (3):
    g0: LineSegment StartX=91.5 StartY=3 StartZ=0 EndX=30 EndY=10 EndZ=0
    g1: LineSegment StartX=30 StartY=10 StartZ=0 EndX=91.5 EndY=10 EndZ=0
    g2: LineSegment StartX=91.5 StartY=10 StartZ=0 EndX=91.5 EndY=3 EndZ=0
  constraints (9):
    c: Coincident(g0,g1)
    c: Horizontal(g1)
    c: Coincident(g1,g2)
    c: Coincident(g2,g0)
    c: Vertical(g2)
    c: DistanceY(g0) = 3
    c: DistanceY(g1) = 10
    c: DistanceX(g1) = 91.5
    c: DistanceX(g0) = 30
FEATURE [PartDesign::Pocket] Pocket003
  BaseFeature = -> Pocket002
  Length = 5
  Length2 = 100
  Midplane = true
  Profile = -> Sketch010
  Type = 1
FEATURE [Mesh::Feature] ferris_wheelring  label="ferris wheelring"
  Placement = pos=(0,-70,0) rot=(0,0,1;3.14159rad)
FEATURE [Sketcher::SketchObject] Sketch011
  FullyConstrained = true
  MapMode = 5
  Support = -> [XY_Plane]
  expr: Constraints[49] = Sketch.Constraints[49]
  expr: Constraints[45] = Sketch.Constraints[45]
  expr: Constraints[33] = Sketch.Constraints[33]
  expr: Constraints[3] = Sketch.Constraints[3]
  expr: Constraints[2] = Sketch.Constraints[2]
  sketch-geometry (21):
    g0: LineSegment StartX=0 StartY=0 StartZ=0 EndX=90 EndY=0 EndZ=0
    g1: LineSegment StartX=10 StartY=-20 StartZ=0 EndX=90 EndY=-70 EndZ=0
    g2: ArcOfCircle CenterX=90 CenterY=0 CenterZ=0 NormalX=0 NormalY=0 NormalZ=1 AngleXU=0 Radius=10 StartAngle=4.71239 EndAngle=7.85398
    g3: ArcOfCircle CenterX=90 CenterY=-70 CenterZ=0 NormalX=0 NormalY=0 NormalZ=1 AngleXU=0 Radius=10 StartAngle=4.15379 EndAngle=7.29538
    g4: ArcOfCircle CenterX=47.7359 CenterY=-20 CenterZ=0 NormalX=0 NormalY=0 NormalZ=1 AngleXU=0 Radius=10 StartAngle=1.5708 EndAngle=4.15379
    g5: ArcOfCircle CenterX=0 CenterY=-37.335 CenterZ=0 NormalX=0 NormalY=0 NormalZ=1 AngleXU=0 Radius=10 StartAngle=1.0122 EndAngle=1.5708
    g6: LineSegment StartX=47.7359 StartY=-10 StartZ=0 EndX=90 EndY=-10 EndZ=0
    g7: LineSegment StartX=42.4359 StartY=-28.48 StartZ=0 EndX=95.3 EndY=-61.52 EndZ=0
    g8: LineSegment StartX=84.7 StartY=-78.48 StartZ=0 EndX=5.29999 EndY=-28.855 EndZ=0
    g9: LineSegment StartX=90 StartY=10 StartZ=0 EndX=31.5 EndY=10 EndZ=0
    g10: LineSegment StartX=0 StartY=10 StartZ=0 EndX=6e-16 EndY=-27.335 EndZ=0
    g11: LineSegment StartX=10 StartY=-20 StartZ=0 EndX=0 EndY=-20 EndZ=0
    g12: LineSegment StartX=90 StartY=0 StartZ=0 EndX=100 EndY=0 EndZ=0
    g13: LineSegment StartX=31.5 StartY=10 StartZ=0 EndX=31.5 EndY=40 EndZ=0
    g14: LineSegment StartX=31.5 StartY=40 StartZ=0 EndX=0 EndY=40 EndZ=0
    g15: LineSegment StartX=0 StartY=40 StartZ=0 EndX=0 EndY=10 EndZ=0
    g16: LineSegment StartX=31.5 StartY=40 StartZ=0 EndX=34.5 EndY=40 EndZ=0
    g17: LineSegment StartX=34.5 StartY=40 StartZ=0 EndX=34.5 EndY=-34.375 EndZ=0
    g18: LineSegment StartX=31.5 StartY=-34.375 StartZ=0 EndX=31.5 EndY=40 EndZ=0
    g19: LineSegment StartX=31.5 StartY=-34.375 StartZ=0 EndX=33 EndY=-34.375 EndZ=0
    g20: LineSegment StartX=33 StartY=-34.375 StartZ=0 EndX=34.5 EndY=-34.375 EndZ=0
  constraints (65):
    c: Coincident(g0,g-1)
    c: PointOnObject(g0,g-1)
    c: DistanceX(g0) = 90
    c: DistanceY(g1) = -70
    c: Vertical(g0,g1)
    c: Coincident(g2,g0)
    c: Coincident(g3,g1)
    c: PointOnObject(g5,g-2)
    c: PointOnObject(g5,g-2)
    c: Coincident(g6,g4)
    c: Coincident(g6,g2)
    c: Horizontal(g6)
    c: Coincident(g7,g4)
    c: Coincident(g7,g3)
    c: Coincident(g8,g3)
    c: Coincident(g8,g5)
    c: Coincident(g9,g2)
    c: PointOnObject(g10,g-2)
    c: Horizontal(g9)
    c: Coincident(g10,g5)
    c: Tangent(g2,g9)
    c: Tangent(g2,g6)
    c: Tangent(g4,g6)
    c: Tangent(g4,g7)
    c: Tangent(g7,g3)
    c: Tangent(g3,g8)
    c: Tangent(g8,g5)
    c: Parallel(g7,g1)
    c: Parallel(g1,g8)
    c: Equal(g5,g3)
    c: Equal(g3,g4)
    c: Equal(g4,g2)
    c: Horizontal(g4,g1)
    c: Diameter(g3) = 20
    c: Coincident(g11,g1)
    c: PointOnObject(g11,g10)
    c: Horizontal(g11)
    c: Coincident(g12,g2)
    c: PointOnObject(g12,g2)
    c: Horizontal(g12)
    c: Equal(g12,g11)
    c: Vertical(g13)
    c: Coincident(g14,g13)
    c: PointOnObject(g14,g-2)
    c: Horizontal(g14)
    c: Distance(g14) = 31.5
    c: Coincident(g15,g14)
    c: Coincident(g15,g10)
    c: Coincident(g9,g13)
    c: Distance(g15) = 30
    c: Horizontal(g10,g9)
    c: Coincident(g16,g17)
    c: Coincident(g18,g16)
    c: Horizontal(g16)
    c: Vertical(g17)
    c: Vertical(g18)
    c: Coincident(g16,g13)
    c: Coincident(g19,g18)
    c: PointOnObject(g19,g1)
    c: Horizontal(g19)
    c: Coincident(g20,g19)
    c: Coincident(g20,g17)
    c: Horizontal(g20)
    c: Equal(g20,g19)
    c: Distance(g16) = 3
FEATURE [Sketcher::SketchObject] Sketch012
  AttachmentOffset = pos=(0,30,0) rot=(0,0,1;0rad)
  FullyConstrained = true
  MapMode = 5
  Placement = pos=(0,30,0) rot=(0,0,1;0rad)
  Support = -> [XY_Plane]
  expr: Constraints[2] = Sketch009.Constraints[2]
  expr: Constraints[1] = Sketch009.Constraints[1]
  expr: Constraints[0] = Sketch009.Constraints[0]
  sketch-geometry (8):
    g0: Circle CenterX=21.9 CenterY=4 CenterZ=0 NormalX=0 NormalY=0 NormalZ=1 AngleXU=0 Radius=2.75
    g1: LineSegment StartX=23.9496 StartY=7.55 StartZ=0 EndX=19.8504 EndY=7.55 EndZ=0
    g2: LineSegment StartX=19.8504 StartY=7.55 StartZ=0 EndX=17.8008 EndY=4 EndZ=0
    g3: LineSegment StartX=17.8008 StartY=4 StartZ=0 EndX=19.8504 EndY=0.45 EndZ=0
    g4: LineSegment StartX=19.8504 StartY=0.45 StartZ=0 EndX=23.9496 EndY=0.45 EndZ=0
    g5: LineSegment StartX=23.9496 StartY=0.45 StartZ=0 EndX=25.9992 EndY=4 EndZ=0
    g6: LineSegment StartX=25.9992 StartY=4 StartZ=0 EndX=23.9496 EndY=7.55 EndZ=0
    g7: Circle CenterX=21.9 CenterY=4 CenterZ=0 NormalX=0 NormalY=0 NormalZ=1 AngleXU=0 Radius=4.09919
  constraints (19):
    c: DistanceX(g0) = 21.9
    c: Diameter(g0) = 5.5
    c: DistanceY(g0) = 4
    c: Coincident(g1,g2)
    c: Coincident(g2,g3)
    c: Coincident(g3,g4)
    c: Coincident(g4,g5)
    c: Coincident(g5,g6)
    c: Coincident(g6,g1)
    c: Equal(g1, g2-g6) x5
    c: PointOnObject(g1,g7)
    c: PointOnObject(g2,g7)
    c: PointOnObject(g3,g7)
    c: PointOnObject(g4,g7)
    c: PointOnObject(g5,g7)
    c: PointOnObject(g6,g7)
    c: Coincident(g7,g0)
    c: Horizontal(g1)
    c: DistanceY(g4,g1) = 7.1
FEATURE [PartDesign::Pocket] Pocket004
  BaseFeature = -> Pocket003
  Length = 4
  Length2 = 100
  Profile = -> Sketch012
  Reversed = true
  Type = 0
FEATURE [Sketcher::SketchObject] Sketch013
  AttachmentOffset = pos=(0,0,31.5) rot=(0,0,1;0rad)
  FullyConstrained = false
  MapMode = 5
  Placement = pos=(31.5,-7e-15,7e-15) rot=(0.57735,0.57735,0.57735;2.0944rad)
  Support = -> [YZ_Plane]
  sketch-geometry (5):
    g0: ArcOfCircle CenterX=34.5199 CenterY=20.7833 CenterZ=0 NormalX=0 NormalY=0 NormalZ=1 AngleXU=0 Radius=5.48009 StartAngle=3.08966e-08 EndAngle=2.02569
    g1: LineSegment StartX=40 StartY=20.7833 StartZ=0 EndX=40 EndY=0 EndZ=0
    g2: LineSegment StartX=32.1121 StartY=25.7062 StartZ=0 EndX=0 EndY=10 EndZ=0
    g3: LineSegment StartX=0 StartY=10 StartZ=0 EndX=0 EndY=0 EndZ=0
    g4: LineSegment StartX=0 StartY=0 StartZ=0 EndX=40 EndY=0 EndZ=0
  constraints (13):
    c: Coincident(g1,g0)
    c: PointOnObject(g1,g-1)
    c: Vertical(g1)
    c: Coincident(g2,g0)
    c: PointOnObject(g2,g-2)
    c: Coincident(g3,g2)
    c: Coincident(g3,g-1)
    c: Coincident(g4,g3)
    c: Coincident(g4,g1)
    c: Tangent(g0,g2)
    c: DistanceY(g2) = 10
    c: DistanceX(g1) = 40
    c: Tangent(g1,g0)
FEATURE [PartDesign::Pad] Pad005
  BaseFeature = -> Pocket004
  Direction = (1,1,1)
  Length = 3
  Length2 = 100
  Profile = -> Sketch013
  Type = 0
FEATURE [PartDesign::Mirrored] Mirrored
  BaseFeature = -> Pad005
  MirrorPlane = -> Sketch [V_Axis]
  Originals = -> [Pad,Pad001,Pad004,Pocket002,Pocket003,Pocket004,Pad005]
FEATURE [PartDesign::Body] Body
  Group = -> [Sketch,Sketch001,Pad,Pad001,Sketch008,Sketch009,Pad004,Pocket002,Sketch010,Pocket003,Sketch011,Sketch012,Pocket004,Sketch013,Pad005,Mirrored]
  Origin = -> Origin
  Tip = -> Mirrored
